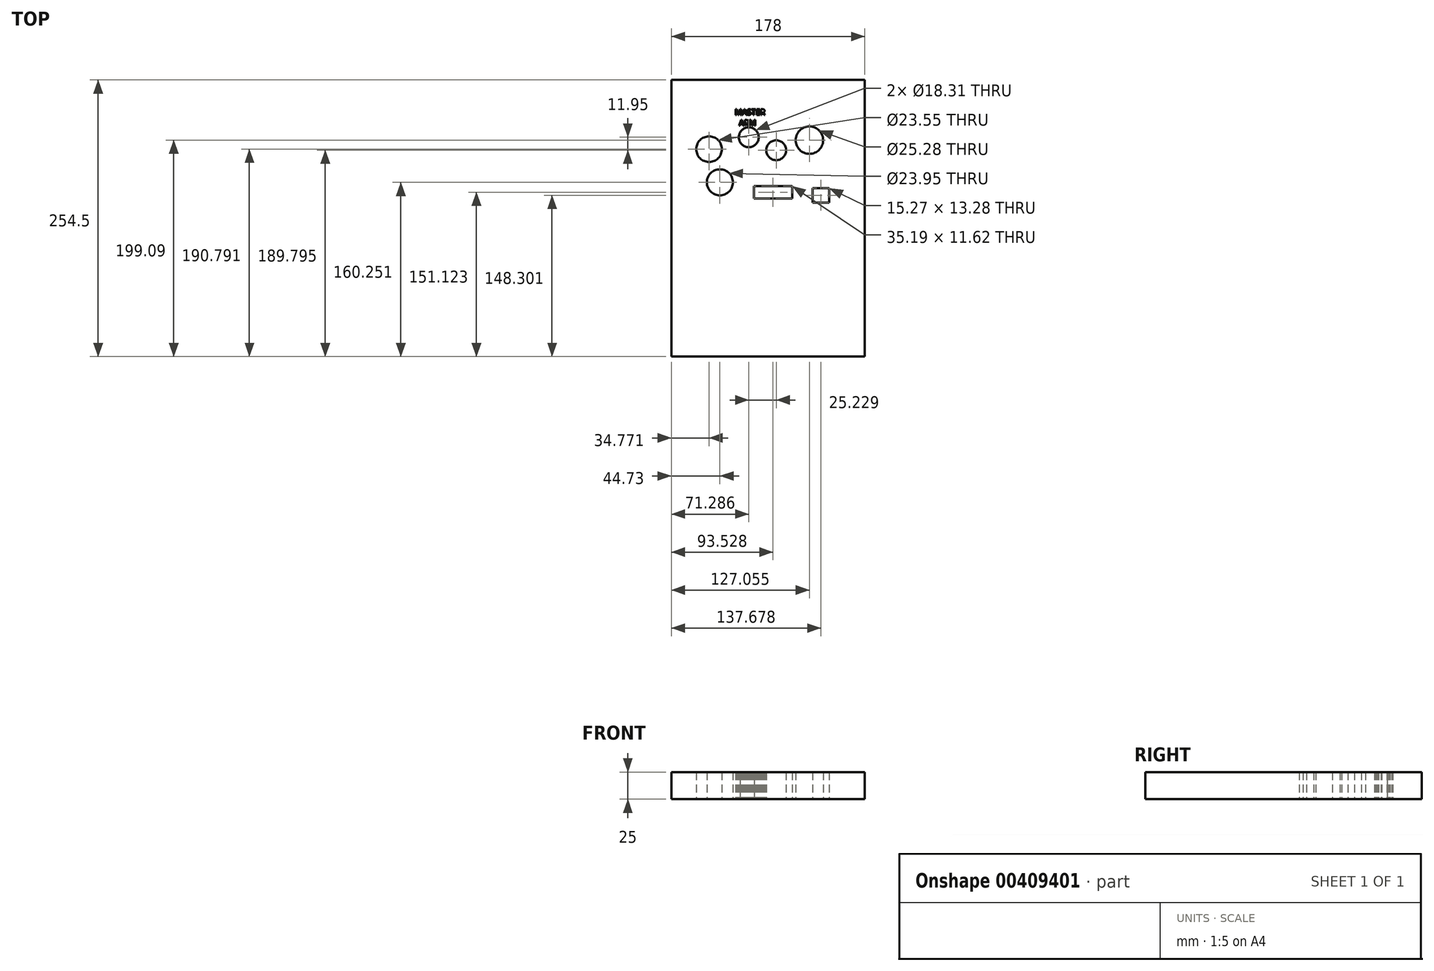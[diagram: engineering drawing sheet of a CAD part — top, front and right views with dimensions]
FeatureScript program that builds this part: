
annotation { "Feature Type Name" : "Feature", "Feature Type Description" : "" }
export const myFeature = defineFeature(function(context is Context, id is Id, definition is map)
    precondition{}
    {
        {
            var Q0;
            Q0=qCreatedBy(makeId("Top.planeOp"),FACE);
            var sketch = newSketch(context, id + "F0", { "sketchPlane" : qUnion([Q0])});
            skLineSegment(sketch, "E0.bottom", {"start": v(-89, 127.25) * mm, "end": v(89, 127.25) * mm});
            skLineSegment(sketch, "E0.top", {"start": v(-89, -127.25) * mm, "end": v(89, -127.25) * mm});
            skLineSegment(sketch, "E0.left", {"start": v(-89, 127.25) * mm, "end": v(-89, -127.25) * mm});
            skLineSegment(sketch, "E0.right", {"start": v(89, 127.25) * mm, "end": v(89, -127.25) * mm});
            skPoint(sketch, "E0.middle", {"position": v(0, 0) * mm});
            skLineSegment(sketch, "E1", {"start": v(-81.78, 42.96) * mm, "end": v(86.19, 42.96) * mm});
            skCircle(sketch, "E2", {"center": v(-54.23, 63.54) * mm, "radius": 11.77 * mm});
            skCircle(sketch, "E3", {"center": v(-17.71, 74.5) * mm, "radius": 9.16 * mm});
            skCircle(sketch, "E4", {"center": v(7.52, 62.55) * mm, "radius": 9.16 * mm});
            skCircle(sketch, "E5", {"center": v(38.06, 71.84) * mm, "radius": 12.64 * mm});
            skCircle(sketch, "E6", {"center": v(-44.27, 33) * mm, "radius": 11.97 * mm});
            skLineSegment(sketch, "E7.bottom", {"start": v(-13.07, 29.68) * mm, "end": v(22.12, 29.68) * mm});
            skLineSegment(sketch, "E7.top", {"start": v(-13.07, 18.06) * mm, "end": v(22.12, 18.06) * mm});
            skLineSegment(sketch, "E7.left", {"start": v(-13.07, 29.68) * mm, "end": v(-13.07, 18.06) * mm});
            skLineSegment(sketch, "E7.right", {"start": v(22.12, 29.68) * mm, "end": v(22.12, 18.06) * mm});
            skLineSegment(sketch, "E8.bottom", {"start": v(41.04, 27.69) * mm, "end": v(56.31, 27.69) * mm});
            skLineSegment(sketch, "E8.top", {"start": v(41.04, 14.41) * mm, "end": v(56.31, 14.41) * mm});
            skLineSegment(sketch, "E8.left", {"start": v(41.04, 27.69) * mm, "end": v(41.04, 14.41) * mm});
            skLineSegment(sketch, "E8.right", {"start": v(56.31, 27.69) * mm, "end": v(56.31, 14.41) * mm});
            skText(sketch, "E9", { "text": "MASTER\n  ARM", "fontName": "OpenSans-Regular.ttf"});
            const initialGuessF0  = {"E9": [-0.03051, 0.0951, 1, 0, 0.00525]};
            skSetInitialGuess(sketch, initialGuessF0);
            skSolve(sketch);
        }
        {
            var Q0;
            Q0=makeQuery(id+"F0.imprint","IMPRINT",FACE,{"disambiguationData":[TD([[makeQuery(id+"F0.imprint","IMPRINT",EDGE,{"derivedFrom":sQuery(id+"F0.wireOp",EDGE,"E0.bottom")}),-1.0]])]});
            extrude(context, id + "F1", {"entities" : qUnion([Q0]), "depth" : 25 * mm});
        }
        {
            var Q0;
            Q0 = qSketchRegion(id + "F0", true);
            extrude(context, id + "F2", {"entities" : qUnion([Q0]), "operationType" : NewBodyOperationType.REMOVE, "oppositeDirection" : true, "depth" : 25 * mm});
        }
    });
